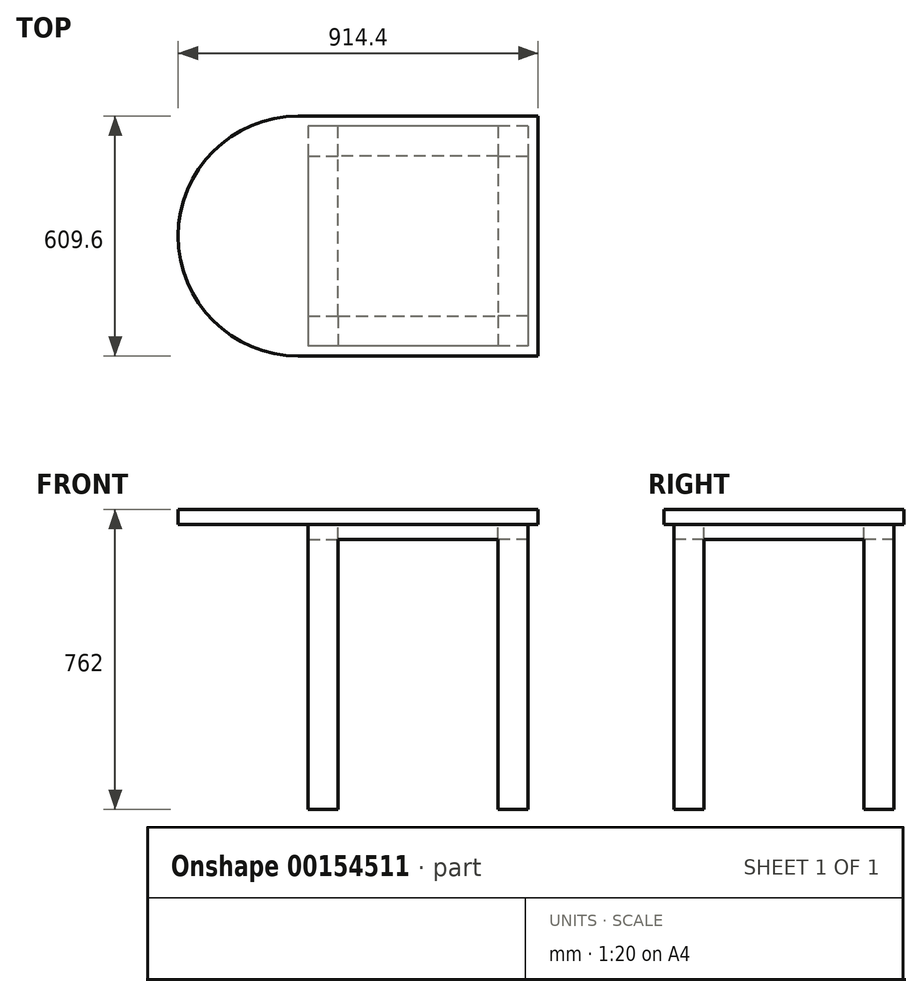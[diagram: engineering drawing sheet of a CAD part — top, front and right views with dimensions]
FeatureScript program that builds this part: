
annotation { "Feature Type Name" : "Feature", "Feature Type Description" : "" }
export const myFeature = defineFeature(function(context is Context, id is Id, definition is map)
    precondition{}
    {
        {
            var Q0;
            Q0=qCreatedBy(makeId("Top.planeOp"),FACE);
            var sketch = newSketch(context, id + "F0", { "sketchPlane" : qUnion([Q0])});
            skLineSegment(sketch, "E0.bottom", {"start": v(304.8, 304.8) * mm, "end": v(-304.8, 304.8) * mm});
            skLineSegment(sketch, "E0.top", {"start": v(304.8, -304.8) * mm, "end": v(-304.8, -304.8) * mm});
            skLineSegment(sketch, "E0.left", {"start": v(304.8, 304.8) * mm, "end": v(304.8, -304.8) * mm});
            skLineSegment(sketch, "E0.right", {"start": v(-304.8, 304.8) * mm, "end": v(-304.8, -304.8) * mm});
            skPoint(sketch, "E0.middle", {"position": v(0, 0) * mm});
            skLineSegment(sketch, "E1.bottom", {"start": v(279.4, 279.4) * mm, "end": v(-279.4, 279.4) * mm});
            skLineSegment(sketch, "E1.top", {"start": v(279.4, -279.4) * mm, "end": v(-279.4, -279.4) * mm});
            skLineSegment(sketch, "E1.left", {"start": v(279.4, 279.4) * mm, "end": v(279.4, -279.4) * mm});
            skLineSegment(sketch, "E1.right", {"start": v(-279.4, 279.4) * mm, "end": v(-279.4, -279.4) * mm});
            skLineSegment(sketch, "E2", {"start": v(-279.4, 203.2) * mm, "end": v(-203.2, 203.2) * mm});
            skLineSegment(sketch, "E3", {"start": v(-203.2, 203.2) * mm, "end": v(-203.2, 279.4) * mm});
            skLineSegment(sketch, "E4", {"start": v(-279.4, -203.2) * mm, "end": v(-203.2, -203.2) * mm});
            skLineSegment(sketch, "E5", {"start": v(-203.2, -203.2) * mm, "end": v(-203.2, -279.4) * mm});
            skLineSegment(sketch, "E6", {"start": v(279.4, -203.2) * mm, "end": v(203.2, -203.2) * mm});
            skLineSegment(sketch, "E7", {"start": v(203.2, -203.2) * mm, "end": v(203.2, -279.4) * mm});
            skLineSegment(sketch, "E8", {"start": v(203.2, 279.4) * mm, "end": v(203.2, 203.2) * mm});
            skLineSegment(sketch, "E9", {"start": v(203.2, 203.2) * mm, "end": v(279.4, 203.2) * mm});
            skLineSegment(sketch, "E10", {"start": v(-203.2, -203.2) * mm, "end": v(-203.2, 203.2) * mm});
            skLineSegment(sketch, "E11", {"start": v(203.2, 203.2) * mm, "end": v(-203.2, 203.2) * mm});
            skLineSegment(sketch, "E12", {"start": v(-203.2, -203.2) * mm, "end": v(203.2, -203.2) * mm});
            skLineSegment(sketch, "E13", {"start": v(203.2, 203.2) * mm, "end": v(203.2, -203.2) * mm});
            skSolve(sketch);
        }
        {
            var Q0;
            Q0=makeQuery(id+"F0.imprint","IMPRINT",FACE,{"disambiguationData":[TD([[makeQuery(id+"F0.imprint","IMPRINT",EDGE,{"derivedFrom":sQuery(id+"F0.wireOp",EDGE,"E0.bottom")}),1.0]])]});
            var Q1;
            {var subQ4=sQuery(id+"F0.wireOp",EDGE,"E2");Q1=makeQuery(id+"F0.imprint","IMPRINT",FACE,{"disambiguationData":[TD([[makeQuery(id+"F0.imprint","IMPRINT",EDGE,{"derivedFrom":subQ4}),1.0]])]});}
            var Q2;
            {var subQ0=sQuery(id+"F0.wireOp",EDGE,"E3");Q2=makeQuery(id+"F0.imprint","IMPRINT",FACE,{"disambiguationData":[TD([[makeQuery(id+"F0.imprint","IMPRINT",EDGE,{"derivedFrom":subQ0}),-1.0]])]});}
            var Q3;
            {var subQ3=sQuery(id+"F0.wireOp",EDGE,"E8");Q3=makeQuery(id+"F0.imprint","IMPRINT",FACE,{"disambiguationData":[TD([[makeQuery(id+"F0.imprint","IMPRINT",EDGE,{"derivedFrom":subQ3}),1.0]])]});}
            var Q4;
            {var subQ0=sQuery(id+"F0.wireOp",EDGE,"E6");Q4=makeQuery(id+"F0.imprint","IMPRINT",FACE,{"disambiguationData":[TD([[makeQuery(id+"F0.imprint","IMPRINT",EDGE,{"derivedFrom":subQ0}),-1.0]])]});}
            var Q5;
            {var subQ4=sQuery(id+"F0.wireOp",EDGE,"E6");Q5=makeQuery(id+"F0.imprint","IMPRINT",FACE,{"disambiguationData":[TD([[makeQuery(id+"F0.imprint","IMPRINT",EDGE,{"derivedFrom":subQ4}),1.0]])]});}
            var Q6;
            {var subQ0=sQuery(id+"F0.wireOp",EDGE,"E5");Q6=makeQuery(id+"F0.imprint","IMPRINT",FACE,{"disambiguationData":[TD([[makeQuery(id+"F0.imprint","IMPRINT",EDGE,{"derivedFrom":subQ0}),1.0]])]});}
            var Q7;
            {var subQ4=sQuery(id+"F0.wireOp",EDGE,"E4");Q7=makeQuery(id+"F0.imprint","IMPRINT",FACE,{"disambiguationData":[TD([[makeQuery(id+"F0.imprint","IMPRINT",EDGE,{"derivedFrom":subQ4}),-1.0]])]});}
            var Q8;
            {var subQ0=sQuery(id+"F0.wireOp",EDGE,"E2");Q8=makeQuery(id+"F0.imprint","IMPRINT",FACE,{"disambiguationData":[TD([[makeQuery(id+"F0.imprint","IMPRINT",EDGE,{"derivedFrom":subQ0}),-1.0]])]});}
            var Q9;
            Q9=makeQuery(id+"F0.imprint","IMPRINT",FACE,{"disambiguationData":[TD([[makeQuery(id+"F0.imprint","IMPRINT",EDGE,{"derivedFrom":sQuery(id+"F0.wireOp",EDGE,"E10")}),-1.0]])]});
            extrude(context, id + "F1", {"entities" : qUnion([Q0, Q1, Q2, Q3, Q4, Q5, Q6, Q7, Q8, Q9]), "oppositeDirection" : true, "depth" : 38.1 * mm});
        }
        {
            var Q0;
            {var subQ4=sQuery(id+"F0.wireOp",EDGE,"E4");Q0=makeQuery(id+"F0.imprint","IMPRINT",FACE,{"disambiguationData":[TD([[makeQuery(id+"F0.imprint","IMPRINT",EDGE,{"derivedFrom":subQ4}),-1.0]])]});}
            var Q1;
            {var subQ0=sQuery(id+"F0.wireOp",EDGE,"E2");Q1=makeQuery(id+"F0.imprint","IMPRINT",FACE,{"disambiguationData":[TD([[makeQuery(id+"F0.imprint","IMPRINT",EDGE,{"derivedFrom":subQ0}),-1.0]])]});}
            var Q2;
            {var subQ0=sQuery(id+"F0.wireOp",EDGE,"E5");Q2=makeQuery(id+"F0.imprint","IMPRINT",FACE,{"disambiguationData":[TD([[makeQuery(id+"F0.imprint","IMPRINT",EDGE,{"derivedFrom":subQ0}),1.0]])]});}
            var Q3;
            {var subQ4=sQuery(id+"F0.wireOp",EDGE,"E6");Q3=makeQuery(id+"F0.imprint","IMPRINT",FACE,{"disambiguationData":[TD([[makeQuery(id+"F0.imprint","IMPRINT",EDGE,{"derivedFrom":subQ4}),1.0]])]});}
            var Q4;
            {var subQ0=sQuery(id+"F0.wireOp",EDGE,"E6");Q4=makeQuery(id+"F0.imprint","IMPRINT",FACE,{"disambiguationData":[TD([[makeQuery(id+"F0.imprint","IMPRINT",EDGE,{"derivedFrom":subQ0}),-1.0]])]});}
            var Q5;
            {var subQ3=sQuery(id+"F0.wireOp",EDGE,"E8");Q5=makeQuery(id+"F0.imprint","IMPRINT",FACE,{"disambiguationData":[TD([[makeQuery(id+"F0.imprint","IMPRINT",EDGE,{"derivedFrom":subQ3}),1.0]])]});}
            var Q6;
            {var subQ0=sQuery(id+"F0.wireOp",EDGE,"E3");Q6=makeQuery(id+"F0.imprint","IMPRINT",FACE,{"disambiguationData":[TD([[makeQuery(id+"F0.imprint","IMPRINT",EDGE,{"derivedFrom":subQ0}),-1.0]])]});}
            var Q7;
            {var subQ4=sQuery(id+"F0.wireOp",EDGE,"E2");Q7=makeQuery(id+"F0.imprint","IMPRINT",FACE,{"disambiguationData":[TD([[makeQuery(id+"F0.imprint","IMPRINT",EDGE,{"derivedFrom":subQ4}),1.0]])]});}
            extrude(context, id + "F2", {"entities" : qUnion([Q0, Q1, Q2, Q3, Q4, Q5, Q6, Q7]), "operationType" : NewBodyOperationType.ADD, "oppositeDirection" : true, "depth" : 76.2 * mm});
        }
        {
            var Q0;
            {var subQ4=sQuery(id+"F0.wireOp",EDGE,"E2");Q0=makeQuery(id+"F0.imprint","IMPRINT",FACE,{"disambiguationData":[TD([[makeQuery(id+"F0.imprint","IMPRINT",EDGE,{"derivedFrom":subQ4}),1.0]])]});}
            var Q1;
            {var subQ4=sQuery(id+"F0.wireOp",EDGE,"E4");Q1=makeQuery(id+"F0.imprint","IMPRINT",FACE,{"disambiguationData":[TD([[makeQuery(id+"F0.imprint","IMPRINT",EDGE,{"derivedFrom":subQ4}),-1.0]])]});}
            var Q2;
            {var subQ4=sQuery(id+"F0.wireOp",EDGE,"E6");Q2=makeQuery(id+"F0.imprint","IMPRINT",FACE,{"disambiguationData":[TD([[makeQuery(id+"F0.imprint","IMPRINT",EDGE,{"derivedFrom":subQ4}),1.0]])]});}
            var Q3;
            {var subQ3=sQuery(id+"F0.wireOp",EDGE,"E8");Q3=makeQuery(id+"F0.imprint","IMPRINT",FACE,{"disambiguationData":[TD([[makeQuery(id+"F0.imprint","IMPRINT",EDGE,{"derivedFrom":subQ3}),1.0]])]});}
            extrude(context, id + "F3", {"entities" : qUnion([Q0, Q1, Q2, Q3]), "operationType" : NewBodyOperationType.ADD, "oppositeDirection" : true, "depth" : 762 * mm});
        }
        {
            var Q0;
            Q0=makeQuery(id+"F1.opExtrude","SWEPT_FACE",FACE,{"disambiguationData":[OSD([sQuery(id+"F0.wireOp",EDGE,"E0.left")])]});
            var sketch = newSketch(context, id + "F4", { "sketchPlane" : qUnion([Q0])});
            skLineSegment(sketch, "E14.bottom", {"start": v(-304.8, 0) * mm, "end": v(304.8, 0) * mm});
            skLineSegment(sketch, "E14.top", {"start": v(-304.8, -38.1) * mm, "end": v(304.8, -38.1) * mm});
            skLineSegment(sketch, "E14.left", {"start": v(-304.8, 0) * mm, "end": v(-304.8, -38.1) * mm});
            skLineSegment(sketch, "E14.right", {"start": v(304.8, 0) * mm, "end": v(304.8, -38.1) * mm});
            skArc(sketch, "E15", {"start": v(-304.8, -38.1) * mm, "mid": v(0, -342.9) * mm, "end": v(304.8, -38.1) * mm});
            skSolve(sketch);
        }
        {
            var Q0;
            Q0=makeQuery(id+"F1.opExtrude","CAP_FACE",FACE,{"disambiguationData":[OSD([sQuery(id+"F0.wireOp",EDGE,"E0.bottom"),sQuery(id+"F0.wireOp",EDGE,"E0.top"),sQuery(id+"F0.wireOp",EDGE,"E0.left"),sQuery(id+"F0.wireOp",EDGE,"E0.right")])],"isStart":true});
            var sketch = newSketch(context, id + "F5", { "sketchPlane" : qUnion([Q0])});
            skLineSegment(sketch, "E16", {"start": v(-304.8, -304.8) * mm, "end": v(-304.8, 304.8) * mm});
            skLineSegment(sketch, "E17", {"start": v(304.8, 304.8) * mm, "end": v(304.8, -304.8) * mm});
            skArc(sketch, "E18", {"start": v(-304.8, 304.8) * mm, "mid": v(-609.6, 0) * mm, "end": v(-304.8, -304.8) * mm});
            skArc(sketch, "E19", {"start": v(304.8, 304.8) * mm, "mid": v(609.6, 0) * mm, "end": v(304.8, -304.8) * mm});
            skSolve(sketch);
        }
        {
            var Q0;
            Q0=makeQuery(id+"F5.imprint","IMPRINT",FACE,{"disambiguationData":[TD([[makeQuery(id+"F5.imprint","IMPRINT",EDGE,{"derivedFrom":sQuery(id+"F5.wireOp",EDGE,"E16")}),-1.0]])]});
            extrude(context, id + "F6", {"entities" : qUnion([Q0]), "operationType" : NewBodyOperationType.ADD, "oppositeDirection" : true, "depth" : 38.1 * mm});
        }
    });
